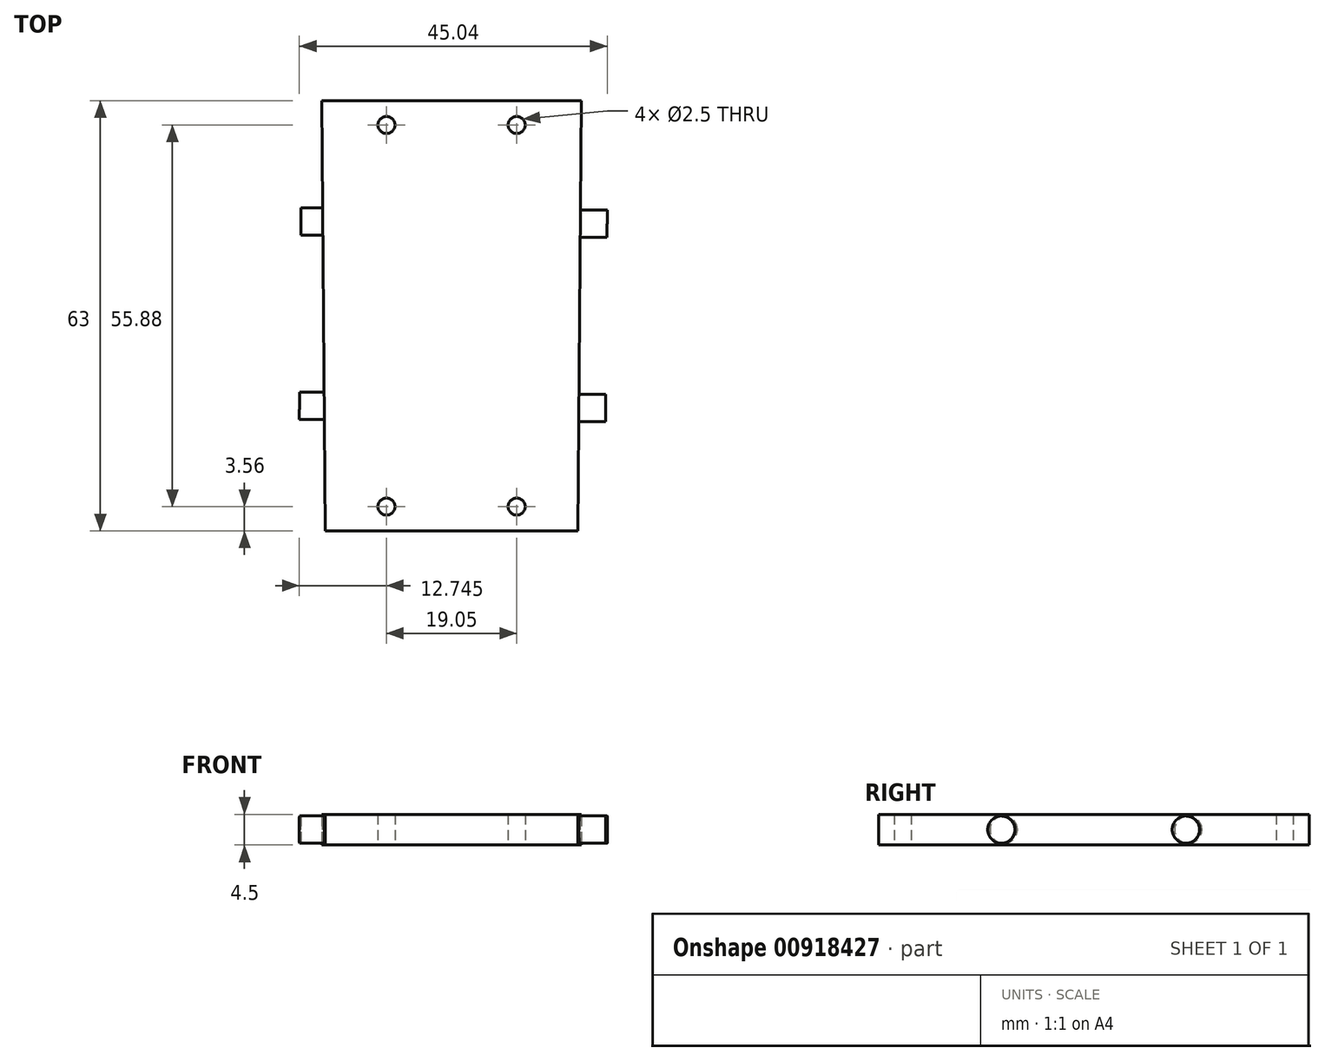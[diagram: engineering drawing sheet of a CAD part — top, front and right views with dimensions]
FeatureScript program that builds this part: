
annotation { "Feature Type Name" : "Feature", "Feature Type Description" : "" }
export const myFeature = defineFeature(function(context is Context, id is Id, definition is map)
    precondition{}
    {
        {
            var Q0;
            Q0=qCreatedBy(makeId("Top.planeOp"),FACE);
            var sketch = newSketch(context, id + "F0", { "sketchPlane" : qUnion([Q0])});
            skLineSegment(sketch, "E0.bottom", {"start": v(-19, 31.5) * mm, "end": v(19, 31.5) * mm});
            skLineSegment(sketch, "E0.top", {"start": v(-18.5, -31.5) * mm, "end": v(18.5, -31.5) * mm});
            skLineSegment(sketch, "E0.left", {"start": v(-19, 31.5) * mm, "end": v(-18.5, -31.5) * mm});
            skLineSegment(sketch, "E0.right", {"start": v(19, 31.5) * mm, "end": v(18.5, -31.5) * mm});
            skPoint(sketch, "E1", {"position": v(0, 31.5) * mm});
            skPoint(sketch, "E2", {"position": v(-18.75, 0) * mm});
            skLineSegment(sketch, "E3.bottom", {"start": v(-9.53, 27.94) * mm, "end": v(9.53, 27.94) * mm, "construction": true});
            skLineSegment(sketch, "E3.top", {"start": v(-9.53, -27.94) * mm, "end": v(9.53, -27.94) * mm, "construction": true});
            skLineSegment(sketch, "E3.left", {"start": v(-9.52, 27.94) * mm, "end": v(-9.53, -27.94) * mm, "construction": true});
            skLineSegment(sketch, "E3.right", {"start": v(9.53, 27.94) * mm, "end": v(9.52, -27.94) * mm, "construction": true});
            skPoint(sketch, "E4", {"position": v(-9.53, 0) * mm});
            skCircle(sketch, "E5", {"center": v(-9.53, 27.94) * mm, "radius": 1.25 * mm});
            skCircle(sketch, "E6", {"center": v(9.53, 27.94) * mm, "radius": 1.25 * mm});
            skCircle(sketch, "E7", {"center": v(9.53, -27.94) * mm, "radius": 1.25 * mm});
            skCircle(sketch, "E8", {"center": v(-9.53, -27.94) * mm, "radius": 1.25 * mm});
            skPoint(sketch, "E9", {"position": v(0, 27.94) * mm});
            skPoint(sketch, "E10", {"position": v(18.75, 0) * mm});
            skPoint(sketch, "E11", {"position": v(0, -31.5) * mm});
            skSolve(sketch);
        }
        {
            var Q0;
            Q0=makeQuery(id+"F0.imprint","IMPRINT",FACE,{"disambiguationData":[TD([[makeQuery(id+"F0.imprint","IMPRINT",EDGE,{"derivedFrom":sQuery(id+"F0.wireOp",EDGE,"E0.bottom")}),-1.0]])]});
            extrude(context, id + "F1", {"entities" : qUnion([Q0]), "depth" : 4.5 * mm, "offsetDistance" : 25 * mm});
        }
        {
            var Q0;
            Q0=makeQuery(id+"F1.opExtrude","SWEPT_FACE",FACE,{"disambiguationData":[OSD([sQuery(id+"F0.wireOp",EDGE,"E0.right")])]});
            cPlane(context, id + "F2", {"entities" : qUnion([Q0]), "cplaneType" : CPlaneType.OFFSET, "offset" : 0 * mm, "width" : 150 * mm, "height" : 150 * mm});
        }
        {
            var Q0;
            Q0=qCreatedBy(id+"F2.planeOp",FACE);
            var sketch = newSketch(context, id + "F3", { "sketchPlane" : qUnion([Q0])});
            skLineSegment(sketch, "E12.0", {"start": v(31.65, 4.5) * mm, "end": v(-31.35, 4.5) * mm, "construction": true});
            skLineSegment(sketch, "E13.0", {"start": v(31.65, 0) * mm, "end": v(-31.35, 0) * mm, "construction": true});
            skLineSegment(sketch, "E14.0", {"start": v(31.65, 4.5) * mm, "end": v(31.65, 0) * mm, "construction": true});
            skLineSegment(sketch, "E15.0", {"start": v(-31.35, 4.5) * mm, "end": v(-31.35, 0) * mm, "construction": true});
            skLineSegment(sketch, "E16", {"start": v(31.65, 2.25) * mm, "end": v(-31.35, 2.25) * mm, "construction": true});
            skCircle(sketch, "E17", {"center": v(13.65, 2.25) * mm, "radius": 2 * mm});
            skCircle(sketch, "E18", {"center": v(-13.35, 2.25) * mm, "radius": 2 * mm});
            skSolve(sketch);
        }
        {
            var Q0;
            Q0=makeQuery(id+"F3.imprint","IMPRINT",FACE,{"disambiguationData":[TD([[makeQuery(id+"F3.imprint","IMPRINT",EDGE,{"derivedFrom":sQuery(id+"F3.wireOp",EDGE,"E17")}),1.0]])]});
            var Q1;
            Q1=makeQuery(id+"F3.imprint","IMPRINT",FACE,{"disambiguationData":[TD([[makeQuery(id+"F3.imprint","IMPRINT",EDGE,{"derivedFrom":sQuery(id+"F3.wireOp",EDGE,"E18")}),1.0]])]});
            extrude(context, id + "F4", {"entities" : qUnion([Q0, Q1]), "operationType" : NewBodyOperationType.ADD, "depth" : 3.9 * mm, "offsetDistance" : 25 * mm, "hasSecondDirection" : true, "secondDirectionOppositeDirection" : true, "secondDirectionDepth" : 40.9 * mm});
        }
    });
